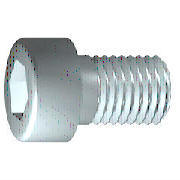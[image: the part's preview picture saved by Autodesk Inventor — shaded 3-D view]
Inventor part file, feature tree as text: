
AUTODESK INVENTOR PART (.ipt)
format: ipt  version: 2013 (Build 170138000, 138)  size: 187,904 bytes
history: native  units: mm (DEFAULTED — no unit token found)
features: sketch x2, extrude x1, plane x1, fillet x1
ambient origin geometry x7: Origin, YZ Plane, XY Plane, X Axis, Y Axis, Z Axis, Center Point
bodies: Solid1 (feature_tree), Body (feature_tree)
feature tree (5):
  extrude  "Slot"  Depth=0.306825mm
  plane  "Work Plane1"
  fillet  "Fillet2"  Radius=3.0mm
  sketch  "Sketch1"  dims[d1=14.693275mm d2=0.306825mm d3=3.0mm]
  sketch  "Sketch2"  dims[d4=1.5mm d5=60.0deg d6=3.0mm d7=3.0mm d8=2.886751mm d9=5.5mm d10=90.0deg d11=10.0mm d12=0.0mm d13=14.693275mm d14=0.0mm d15=0.306725mm d16=0.306725mm d17=0.3mm d19=0.0mm d26=16.0mm d27=45.0deg d28=0.0mm d29=0.0mm d30=0.1mm]
